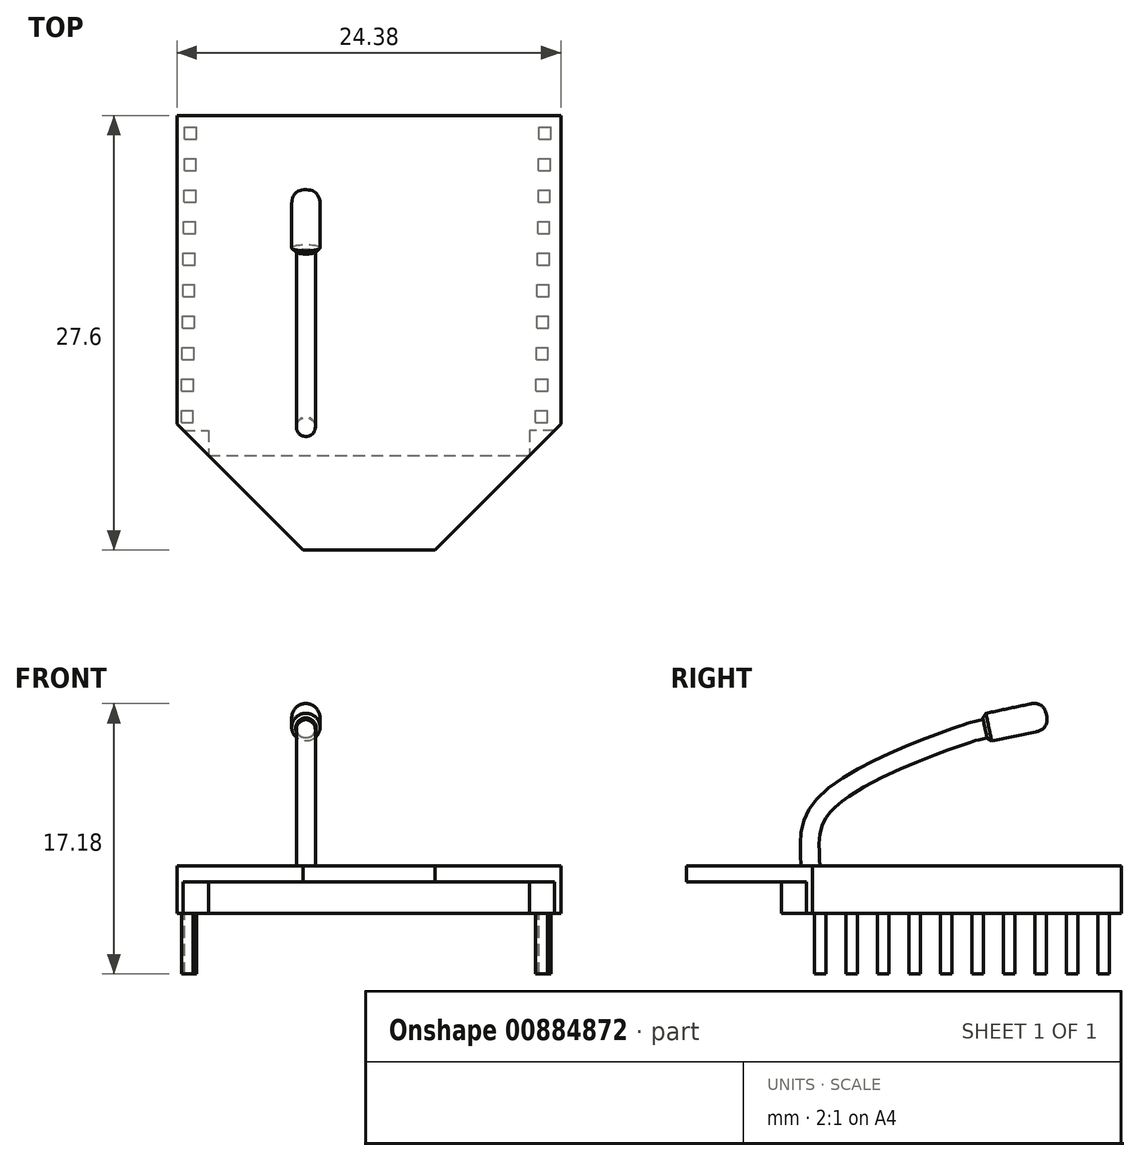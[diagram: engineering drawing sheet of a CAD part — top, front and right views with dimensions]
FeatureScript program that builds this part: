
annotation { "Feature Type Name" : "Feature", "Feature Type Description" : "" }
export const myFeature = defineFeature(function(context is Context, id is Id, definition is map)
    precondition{}
    {
        {
            var Q0;
            Q0=qCreatedBy(makeId("Top.planeOp"),FACE);
            var sketch = newSketch(context, id + "F0", { "sketchPlane" : qUnion([Q0])});
            skLineSegment(sketch, "E0.bottom", {"start": v(-12.19, 13.8) * mm, "end": v(12.2, 13.8) * mm});
            skLineSegment(sketch, "E0.top", {"start": v(-12.2, -13.8) * mm, "end": v(12.2, -13.8) * mm});
            skLineSegment(sketch, "E0.left", {"start": v(-12.19, 13.8) * mm, "end": v(-12.2, -13.8) * mm});
            skLineSegment(sketch, "E0.right", {"start": v(12.2, 13.8) * mm, "end": v(12.19, -13.8) * mm});
            skPoint(sketch, "E0.middle", {"position": v(0, 0) * mm});
            skSolve(sketch);
        }
        {
            var Q0;
            Q0=qSketchRegion(id+"F0",true);
            extrude(context, id + "F1", {"entities" : qUnion([Q0]), "oppositeDirection" : true, "depth" : 1 * mm, "offsetDistance" : 25 * mm});
        }
        {
            var Q0;
            Q0=makeQuery(id+"F1.opExtrude","CAP_FACE",FACE,{"disambiguationData":[OSD([sQuery(id+"F0.wireOp",EDGE,"E0.bottom"),sQuery(id+"F0.wireOp",EDGE,"E0.top"),sQuery(id+"F0.wireOp",EDGE,"E0.left"),sQuery(id+"F0.wireOp",EDGE,"E0.right")])],"isStart":false});
            var sketch = newSketch(context, id + "F2", { "sketchPlane" : qUnion([Q0])});
            skLineSegment(sketch, "E1.bottom", {"start": v(-12.19, -13.8) * mm, "end": v(-10.19, -13.8) * mm});
            skLineSegment(sketch, "E1.top", {"start": v(-12.2, 6.2) * mm, "end": v(-10.2, 6.2) * mm});
            skLineSegment(sketch, "E1.left", {"start": v(-12.19, -13.8) * mm, "end": v(-12.19, 6.2) * mm});
            skLineSegment(sketch, "E1.right", {"start": v(-10.19, -13.8) * mm, "end": v(-10.2, 6.2) * mm});
            skLineSegment(sketch, "E2.bottom", {"start": v(12.2, -13.8) * mm, "end": v(10.2, -13.8) * mm});
            skLineSegment(sketch, "E2.top", {"start": v(12.2, 6.2) * mm, "end": v(10.2, 6.2) * mm});
            skLineSegment(sketch, "E2.left", {"start": v(12.2, -13.8) * mm, "end": v(12.2, 6.2) * mm});
            skLineSegment(sketch, "E2.right", {"start": v(10.2, -13.8) * mm, "end": v(10.2, 6.2) * mm});
            skSolve(sketch);
        }
        {
            var Q0;
            Q0=makeQuery(id+"F2.imprint","IMPRINT",FACE,{"disambiguationData":[TD([[makeQuery(id+"F2.imprint","IMPRINT",EDGE,{"derivedFrom":sQuery(id+"F2.wireOp",EDGE,"E1.bottom")}),1.0]])]});
            var Q1;
            Q1=makeQuery(id+"F2.imprint","IMPRINT",FACE,{"disambiguationData":[TD([[makeQuery(id+"F2.imprint","IMPRINT",EDGE,{"derivedFrom":sQuery(id+"F2.wireOp",EDGE,"E2.bottom")}),1.0]])]});
            extrude(context, id + "F3", {"entities" : qUnion([Q0, Q1]), "operationType" : NewBodyOperationType.ADD, "depth" : 2 * mm, "offsetDistance" : 25 * mm});
        }
        {
            var Q0;
            Q0=makeQuery(id+"F3.opExtrude","CAP_FACE",FACE,{"disambiguationData":[OSD([sQuery(id+"F2.wireOp",EDGE,"E1.bottom"),sQuery(id+"F2.wireOp",EDGE,"E1.top"),sQuery(id+"F2.wireOp",EDGE,"E1.left"),sQuery(id+"F2.wireOp",EDGE,"E1.right")])],"isStart":false});
            var sketch = newSketch(context, id + "F4", { "sketchPlane" : qUnion([Q0])});
            skLineSegment(sketch, "E3.bottom", {"start": v(-11.69, -12.3) * mm, "end": v(-10.94, -12.3) * mm});
            skLineSegment(sketch, "E3.top", {"start": v(-11.69, -13.05) * mm, "end": v(-10.94, -13.05) * mm});
            skLineSegment(sketch, "E3.left", {"start": v(-11.69, -12.3) * mm, "end": v(-11.69, -13.05) * mm});
            skLineSegment(sketch, "E3.right", {"start": v(-10.94, -12.3) * mm, "end": v(-10.94, -13.05) * mm});
            skLineSegment(sketch, "E4.0.1.0", {"start": v(-11.71, -10.3) * mm, "end": v(-10.96, -10.3) * mm});
            skLineSegment(sketch, "E4.0.1.1", {"start": v(-10.96, -10.3) * mm, "end": v(-10.96, -11.06) * mm});
            skLineSegment(sketch, "E4.0.1.2", {"start": v(-11.71, -10.3) * mm, "end": v(-11.71, -11.06) * mm});
            skLineSegment(sketch, "E4.0.1.3", {"start": v(-11.71, -11.06) * mm, "end": v(-10.96, -11.06) * mm});
            skLineSegment(sketch, "E4.0.2.0", {"start": v(-11.74, -8.3) * mm, "end": v(-10.99, -8.3) * mm});
            skLineSegment(sketch, "E4.0.2.1", {"start": v(-10.99, -8.3) * mm, "end": v(-10.99, -9.06) * mm});
            skLineSegment(sketch, "E4.0.2.2", {"start": v(-11.74, -8.3) * mm, "end": v(-11.74, -9.06) * mm});
            skLineSegment(sketch, "E4.0.2.3", {"start": v(-11.74, -9.06) * mm, "end": v(-10.99, -9.06) * mm});
            skLineSegment(sketch, "E4.0.3.0", {"start": v(-11.76, -6.3) * mm, "end": v(-11.01, -6.3) * mm});
            skLineSegment(sketch, "E4.0.3.1", {"start": v(-11.01, -6.3) * mm, "end": v(-11.01, -7.06) * mm});
            skLineSegment(sketch, "E4.0.3.2", {"start": v(-11.76, -6.3) * mm, "end": v(-11.76, -7.06) * mm});
            skLineSegment(sketch, "E4.0.3.3", {"start": v(-11.76, -7.06) * mm, "end": v(-11.01, -7.06) * mm});
            skLineSegment(sketch, "E4.0.4.0", {"start": v(-11.79, -4.3) * mm, "end": v(-11.04, -4.3) * mm});
            skLineSegment(sketch, "E4.0.4.1", {"start": v(-11.04, -4.3) * mm, "end": v(-11.04, -5.06) * mm});
            skLineSegment(sketch, "E4.0.4.2", {"start": v(-11.79, -4.3) * mm, "end": v(-11.79, -5.06) * mm});
            skLineSegment(sketch, "E4.0.4.3", {"start": v(-11.79, -5.06) * mm, "end": v(-11.04, -5.06) * mm});
            skLineSegment(sketch, "E4.0.5.0", {"start": v(-11.81, -2.3) * mm, "end": v(-11.06, -2.3) * mm});
            skLineSegment(sketch, "E4.0.5.1", {"start": v(-11.06, -2.3) * mm, "end": v(-11.06, -3.06) * mm});
            skLineSegment(sketch, "E4.0.5.2", {"start": v(-11.81, -2.3) * mm, "end": v(-11.81, -3.06) * mm});
            skLineSegment(sketch, "E4.0.5.3", {"start": v(-11.81, -3.06) * mm, "end": v(-11.06, -3.06) * mm});
            skLineSegment(sketch, "E4.0.6.0", {"start": v(-11.83, -0.3) * mm, "end": v(-11.08, -0.3) * mm});
            skLineSegment(sketch, "E4.0.6.1", {"start": v(-11.08, -0.3) * mm, "end": v(-11.08, -1.06) * mm});
            skLineSegment(sketch, "E4.0.6.2", {"start": v(-11.83, -0.3) * mm, "end": v(-11.83, -1.06) * mm});
            skLineSegment(sketch, "E4.0.6.3", {"start": v(-11.83, -1.06) * mm, "end": v(-11.08, -1.06) * mm});
            skLineSegment(sketch, "E4.0.7.0", {"start": v(-11.86, 1.7) * mm, "end": v(-11.1, 1.7) * mm});
            skLineSegment(sketch, "E4.0.7.1", {"start": v(-11.1, 1.7) * mm, "end": v(-11.1, 0.94) * mm});
            skLineSegment(sketch, "E4.0.7.2", {"start": v(-11.86, 1.7) * mm, "end": v(-11.86, 0.94) * mm});
            skLineSegment(sketch, "E4.0.7.3", {"start": v(-11.86, 0.94) * mm, "end": v(-11.1, 0.94) * mm});
            skLineSegment(sketch, "E4.0.8.0", {"start": v(-11.88, 3.7) * mm, "end": v(-11.13, 3.7) * mm});
            skLineSegment(sketch, "E4.0.8.1", {"start": v(-11.13, 3.7) * mm, "end": v(-11.13, 2.94) * mm});
            skLineSegment(sketch, "E4.0.8.2", {"start": v(-11.88, 3.7) * mm, "end": v(-11.88, 2.94) * mm});
            skLineSegment(sketch, "E4.0.8.3", {"start": v(-11.88, 2.94) * mm, "end": v(-11.13, 2.94) * mm});
            skLineSegment(sketch, "E4.0.9.0", {"start": v(-11.9, 5.7) * mm, "end": v(-11.16, 5.7) * mm});
            skLineSegment(sketch, "E4.0.9.1", {"start": v(-11.16, 5.7) * mm, "end": v(-11.16, 4.94) * mm});
            skLineSegment(sketch, "E4.0.9.2", {"start": v(-11.9, 5.7) * mm, "end": v(-11.9, 4.94) * mm});
            skLineSegment(sketch, "E4.0.9.3", {"start": v(-11.9, 4.94) * mm, "end": v(-11.16, 4.94) * mm});
            skLineSegment(sketch, "E4.1.0.0", {"start": v(10.81, -12.3) * mm, "end": v(11.56, -12.3) * mm});
            skLineSegment(sketch, "E4.1.0.1", {"start": v(11.56, -12.3) * mm, "end": v(11.56, -13.05) * mm});
            skLineSegment(sketch, "E4.1.0.2", {"start": v(10.81, -12.3) * mm, "end": v(10.81, -13.05) * mm});
            skLineSegment(sketch, "E4.1.0.3", {"start": v(10.81, -13.05) * mm, "end": v(11.56, -13.05) * mm});
            skLineSegment(sketch, "E4.1.1.0", {"start": v(10.79, -10.3) * mm, "end": v(11.54, -10.3) * mm});
            skLineSegment(sketch, "E4.1.1.1", {"start": v(11.54, -10.3) * mm, "end": v(11.54, -11.06) * mm});
            skLineSegment(sketch, "E4.1.1.2", {"start": v(10.79, -10.3) * mm, "end": v(10.79, -11.06) * mm});
            skLineSegment(sketch, "E4.1.1.3", {"start": v(10.79, -11.06) * mm, "end": v(11.54, -11.06) * mm});
            skLineSegment(sketch, "E4.1.2.0", {"start": v(10.76, -8.3) * mm, "end": v(11.51, -8.3) * mm});
            skLineSegment(sketch, "E4.1.2.1", {"start": v(11.51, -8.3) * mm, "end": v(11.51, -9.06) * mm});
            skLineSegment(sketch, "E4.1.2.2", {"start": v(10.76, -8.3) * mm, "end": v(10.76, -9.06) * mm});
            skLineSegment(sketch, "E4.1.2.3", {"start": v(10.76, -9.06) * mm, "end": v(11.51, -9.06) * mm});
            skLineSegment(sketch, "E4.1.3.0", {"start": v(10.74, -6.3) * mm, "end": v(11.49, -6.3) * mm});
            skLineSegment(sketch, "E4.1.3.1", {"start": v(11.49, -6.3) * mm, "end": v(11.49, -7.06) * mm});
            skLineSegment(sketch, "E4.1.3.2", {"start": v(10.74, -6.3) * mm, "end": v(10.74, -7.06) * mm});
            skLineSegment(sketch, "E4.1.3.3", {"start": v(10.74, -7.06) * mm, "end": v(11.49, -7.06) * mm});
            skLineSegment(sketch, "E4.1.4.0", {"start": v(10.71, -4.3) * mm, "end": v(11.46, -4.3) * mm});
            skLineSegment(sketch, "E4.1.4.1", {"start": v(11.46, -4.3) * mm, "end": v(11.46, -5.06) * mm});
            skLineSegment(sketch, "E4.1.4.2", {"start": v(10.71, -4.3) * mm, "end": v(10.71, -5.06) * mm});
            skLineSegment(sketch, "E4.1.4.3", {"start": v(10.71, -5.06) * mm, "end": v(11.46, -5.06) * mm});
            skLineSegment(sketch, "E4.1.5.0", {"start": v(10.69, -2.3) * mm, "end": v(11.44, -2.3) * mm});
            skLineSegment(sketch, "E4.1.5.1", {"start": v(11.44, -2.3) * mm, "end": v(11.44, -3.06) * mm});
            skLineSegment(sketch, "E4.1.5.2", {"start": v(10.69, -2.3) * mm, "end": v(10.69, -3.06) * mm});
            skLineSegment(sketch, "E4.1.5.3", {"start": v(10.69, -3.06) * mm, "end": v(11.44, -3.06) * mm});
            skLineSegment(sketch, "E4.1.6.0", {"start": v(10.67, -0.3) * mm, "end": v(11.42, -0.3) * mm});
            skLineSegment(sketch, "E4.1.6.1", {"start": v(11.42, -0.3) * mm, "end": v(11.42, -1.06) * mm});
            skLineSegment(sketch, "E4.1.6.2", {"start": v(10.67, -0.3) * mm, "end": v(10.67, -1.06) * mm});
            skLineSegment(sketch, "E4.1.6.3", {"start": v(10.67, -1.06) * mm, "end": v(11.42, -1.06) * mm});
            skLineSegment(sketch, "E4.1.7.0", {"start": v(10.64, 1.7) * mm, "end": v(11.4, 1.7) * mm});
            skLineSegment(sketch, "E4.1.7.1", {"start": v(11.4, 1.7) * mm, "end": v(11.4, 0.94) * mm});
            skLineSegment(sketch, "E4.1.7.2", {"start": v(10.64, 1.7) * mm, "end": v(10.64, 0.94) * mm});
            skLineSegment(sketch, "E4.1.7.3", {"start": v(10.64, 0.94) * mm, "end": v(11.4, 0.94) * mm});
            skLineSegment(sketch, "E4.1.8.0", {"start": v(10.62, 3.7) * mm, "end": v(11.37, 3.7) * mm});
            skLineSegment(sketch, "E4.1.8.1", {"start": v(11.37, 3.7) * mm, "end": v(11.37, 2.94) * mm});
            skLineSegment(sketch, "E4.1.8.2", {"start": v(10.62, 3.7) * mm, "end": v(10.62, 2.94) * mm});
            skLineSegment(sketch, "E4.1.8.3", {"start": v(10.62, 2.94) * mm, "end": v(11.37, 2.94) * mm});
            skLineSegment(sketch, "E4.1.9.0", {"start": v(10.6, 5.7) * mm, "end": v(11.34, 5.7) * mm});
            skLineSegment(sketch, "E4.1.9.1", {"start": v(11.34, 5.7) * mm, "end": v(11.34, 4.94) * mm});
            skLineSegment(sketch, "E4.1.9.2", {"start": v(10.6, 5.7) * mm, "end": v(10.6, 4.94) * mm});
            skLineSegment(sketch, "E4.1.9.3", {"start": v(10.6, 4.94) * mm, "end": v(11.34, 4.94) * mm});
            skLineSegment(sketch, "E4.direction1", {"start": v(-11.69, -13.05) * mm, "end": v(10.81, -13.05) * mm, "construction": true});
            skLineSegment(sketch, "E4.direction2", {"start": v(-11.69, -13.05) * mm, "end": v(-11.71, -11.06) * mm, "construction": true});
            skSolve(sketch);
        }
        {
            var Q0;
            Q0=makeQuery(id+"F4.imprint","IMPRINT",FACE,{"disambiguationData":[TD([[makeQuery(id+"F4.imprint","IMPRINT",EDGE,{"derivedFrom":sQuery(id+"F4.wireOp",EDGE,"E3.bottom")}),-1.0]])]});
            var Q1;
            Q1=makeQuery(id+"F4.imprint","IMPRINT",FACE,{"disambiguationData":[TD([[makeQuery(id+"F4.imprint","IMPRINT",EDGE,{"derivedFrom":sQuery(id+"F4.wireOp",EDGE,"E4.0.1.0")}),-1.0]])]});
            var Q2;
            Q2=makeQuery(id+"F4.imprint","IMPRINT",FACE,{"disambiguationData":[TD([[makeQuery(id+"F4.imprint","IMPRINT",EDGE,{"derivedFrom":sQuery(id+"F4.wireOp",EDGE,"E4.0.2.0")}),-1.0]])]});
            var Q3;
            Q3=makeQuery(id+"F4.imprint","IMPRINT",FACE,{"disambiguationData":[TD([[makeQuery(id+"F4.imprint","IMPRINT",EDGE,{"derivedFrom":sQuery(id+"F4.wireOp",EDGE,"E4.0.3.0")}),-1.0]])]});
            var Q4;
            Q4=makeQuery(id+"F4.imprint","IMPRINT",FACE,{"disambiguationData":[TD([[makeQuery(id+"F4.imprint","IMPRINT",EDGE,{"derivedFrom":sQuery(id+"F4.wireOp",EDGE,"E4.0.4.0")}),-1.0]])]});
            var Q5;
            Q5=makeQuery(id+"F4.imprint","IMPRINT",FACE,{"disambiguationData":[TD([[makeQuery(id+"F4.imprint","IMPRINT",EDGE,{"derivedFrom":sQuery(id+"F4.wireOp",EDGE,"E4.0.5.0")}),-1.0]])]});
            var Q6;
            Q6=makeQuery(id+"F4.imprint","IMPRINT",FACE,{"disambiguationData":[TD([[makeQuery(id+"F4.imprint","IMPRINT",EDGE,{"derivedFrom":sQuery(id+"F4.wireOp",EDGE,"E4.0.6.0")}),-1.0]])]});
            var Q7;
            Q7=makeQuery(id+"F4.imprint","IMPRINT",FACE,{"disambiguationData":[TD([[makeQuery(id+"F4.imprint","IMPRINT",EDGE,{"derivedFrom":sQuery(id+"F4.wireOp",EDGE,"E4.0.7.0")}),-1.0]])]});
            var Q8;
            Q8=makeQuery(id+"F4.imprint","IMPRINT",FACE,{"disambiguationData":[TD([[makeQuery(id+"F4.imprint","IMPRINT",EDGE,{"derivedFrom":sQuery(id+"F4.wireOp",EDGE,"E4.0.8.0")}),-1.0]])]});
            var Q9;
            Q9=makeQuery(id+"F4.imprint","IMPRINT",FACE,{"disambiguationData":[TD([[makeQuery(id+"F4.imprint","IMPRINT",EDGE,{"derivedFrom":sQuery(id+"F4.wireOp",EDGE,"E4.0.9.0")}),-1.0]])]});
            var Q10;
            Q10=makeQuery(id+"F4.imprint","IMPRINT",FACE,{"disambiguationData":[TD([[makeQuery(id+"F4.imprint","IMPRINT",EDGE,{"derivedFrom":sQuery(id+"F4.wireOp",EDGE,"E4.1.9.0")}),-1.0]])]});
            var Q11;
            Q11=makeQuery(id+"F4.imprint","IMPRINT",FACE,{"disambiguationData":[TD([[makeQuery(id+"F4.imprint","IMPRINT",EDGE,{"derivedFrom":sQuery(id+"F4.wireOp",EDGE,"E4.1.8.0")}),-1.0]])]});
            var Q12;
            Q12=makeQuery(id+"F4.imprint","IMPRINT",FACE,{"disambiguationData":[TD([[makeQuery(id+"F4.imprint","IMPRINT",EDGE,{"derivedFrom":sQuery(id+"F4.wireOp",EDGE,"E4.1.7.0")}),-1.0]])]});
            var Q13;
            Q13=makeQuery(id+"F4.imprint","IMPRINT",FACE,{"disambiguationData":[TD([[makeQuery(id+"F4.imprint","IMPRINT",EDGE,{"derivedFrom":sQuery(id+"F4.wireOp",EDGE,"E4.1.6.0")}),-1.0]])]});
            var Q14;
            Q14=makeQuery(id+"F4.imprint","IMPRINT",FACE,{"disambiguationData":[TD([[makeQuery(id+"F4.imprint","IMPRINT",EDGE,{"derivedFrom":sQuery(id+"F4.wireOp",EDGE,"E4.1.5.0")}),-1.0]])]});
            var Q15;
            Q15=makeQuery(id+"F4.imprint","IMPRINT",FACE,{"disambiguationData":[TD([[makeQuery(id+"F4.imprint","IMPRINT",EDGE,{"derivedFrom":sQuery(id+"F4.wireOp",EDGE,"E4.1.4.0")}),-1.0]])]});
            var Q16;
            Q16=makeQuery(id+"F4.imprint","IMPRINT",FACE,{"disambiguationData":[TD([[makeQuery(id+"F4.imprint","IMPRINT",EDGE,{"derivedFrom":sQuery(id+"F4.wireOp",EDGE,"E4.1.3.0")}),-1.0]])]});
            var Q17;
            Q17=makeQuery(id+"F4.imprint","IMPRINT",FACE,{"disambiguationData":[TD([[makeQuery(id+"F4.imprint","IMPRINT",EDGE,{"derivedFrom":sQuery(id+"F4.wireOp",EDGE,"E4.1.2.0")}),-1.0]])]});
            var Q18;
            Q18=makeQuery(id+"F4.imprint","IMPRINT",FACE,{"disambiguationData":[TD([[makeQuery(id+"F4.imprint","IMPRINT",EDGE,{"derivedFrom":sQuery(id+"F4.wireOp",EDGE,"E4.1.1.0")}),-1.0]])]});
            var Q19;
            Q19=makeQuery(id+"F4.imprint","IMPRINT",FACE,{"disambiguationData":[TD([[makeQuery(id+"F4.imprint","IMPRINT",EDGE,{"derivedFrom":sQuery(id+"F4.wireOp",EDGE,"E4.1.0.0")}),-1.0]])]});
            extrude(context, id + "F5", {"entities" : qUnion([Q0, Q1, Q2, Q3, Q4, Q5, Q6, Q7, Q8, Q9, Q10, Q11, Q12, Q13, Q14, Q15, Q16, Q17, Q18, Q19]), "operationType" : NewBodyOperationType.ADD, "depth" : (6.86 - (1 + 2)) * mm, "offsetDistance" : 25 * mm});
        }
        {
            var Q0;
            Q0=makeQuery(id+"F1.opExtrude","SWEPT_EDGE",EDGE,{"disambiguationData":[OSD([sQuery(id+"F0.wireOp",EDGE,"E0.top"),sQuery(id+"F0.wireOp",EDGE,"E0.right")])]});
            var Q1;
            Q1=makeQuery(id+"F1.opExtrude","SWEPT_EDGE",EDGE,{"disambiguationData":[OSD([sQuery(id+"F0.wireOp",EDGE,"E0.top"),sQuery(id+"F0.wireOp",EDGE,"E0.left")])]});
            chamfer(context, id + "F6", {"entities" : qUnion([Q0, Q1]), "width" : 8 * mm, "tangentPropagation" : true});
        }
        {
            var Q0;
            Q0=makeQuery(id+"F1.opExtrude","CAP_FACE",FACE,{"disambiguationData":[OSD([sQuery(id+"F0.wireOp",EDGE,"E0.bottom"),sQuery(id+"F0.wireOp",EDGE,"E0.top"),sQuery(id+"F0.wireOp",EDGE,"E0.left"),sQuery(id+"F0.wireOp",EDGE,"E0.right")])],"isStart":false});
            var sketch = newSketch(context, id + "F7", { "sketchPlane" : qUnion([Q0])});
            skLineSegment(sketch, "E5.bottom", {"start": v(-10.19, -13.8) * mm, "end": v(10.2, -13.8) * mm});
            skLineSegment(sketch, "E5.top", {"start": v(-10.19, 7.8) * mm, "end": v(10.2, 7.8) * mm});
            skLineSegment(sketch, "E5.left", {"start": v(-10.2, -13.8) * mm, "end": v(-10.2, 7.8) * mm});
            skLineSegment(sketch, "E5.right", {"start": v(10.2, -13.8) * mm, "end": v(10.2, 7.8) * mm});
            skSolve(sketch);
        }
        {
            var Q0;
            {var subQ2=sQuery(id+"F7.wireOp",EDGE,"E5.top");Q0=makeQuery(id+"F7.imprint","IMPRINT",FACE,{"disambiguationData":[TD([[makeQuery(id+"F7.imprint","IMPRINT",EDGE,{"derivedFrom":subQ2}),-1.0]])]});}
            extrude(context, id + "F8", {"entities" : qUnion([Q0]), "operationType" : NewBodyOperationType.ADD, "depth" : 2 * mm, "offsetDistance" : 25 * mm});
        }
        {
            var Q0;
            Q0=qCreatedBy(makeId("Right.planeOp"),FACE);
            cPlane(context, id + "F9", {"entities" : qUnion([Q0]), "cplaneType" : CPlaneType.OFFSET, "offset" : 4 * mm, "oppositeDirection" : true, "width" : 150 * mm, "height" : 150 * mm});
        }
        {
            var Q0;
            Q0=qCreatedBy(id+"F9.planeOp",FACE);
            var sketch = newSketch(context, id + "F10", { "sketchPlane" : qUnion([Q0])});
            skFitSpline(sketch, "E6", {"points": [v(-5.95, 0) * mm, v(-4.96, 4) * mm, v(3.85, 8.37) * mm, v(9.06, 9.6) * mm], "startDerivative": vector(-0.35, 15.25) * mm, "endDerivative": vector(50.53, 11.9) * mm});
            skSolve(sketch);
        }
        {
            var Q0;
            Q0=makeQuery(id+"F1.opExtrude","CAP_FACE",FACE,{"disambiguationData":[OSD([sQuery(id+"F0.wireOp",EDGE,"E0.bottom"),sQuery(id+"F0.wireOp",EDGE,"E0.top"),sQuery(id+"F0.wireOp",EDGE,"E0.left"),sQuery(id+"F0.wireOp",EDGE,"E0.right")])],"isStart":true});
            var sketch = newSketch(context, id + "F11", { "sketchPlane" : qUnion([Q0])});
            skCircle(sketch, "E7", {"center": v(-4, -5.95) * mm, "radius": 0.6 * mm});
            skSolve(sketch);
        }
        {
            var Q0;
            Q0=makeQuery(id+"F11.imprint","IMPRINT",FACE,{"disambiguationData":[TD([[makeQuery(id+"F11.imprint","IMPRINT",EDGE,{"derivedFrom":sQuery(id+"F11.wireOp",EDGE,"E7")}),1.0]])]});
            var Q1;
            Q1=sQuery(id+"F10.wireOp",EDGE,"E6");
            sweep(context, id + "F12", {"operationType" : NewBodyOperationType.ADD, "profiles" : qUnion([Q0]), "path" : qUnion([Q1])});
        }
        {
            var Q0;
            Q0=makeQuery(id+"F12.opSweep","CAP_FACE",FACE,{"disambiguationData":[OSD([sQuery(id+"F10.wireOp",VERTEX,"E6.end"),sQuery(id+"F11.wireOp",EDGE,"E7")])],"isStart":false});
            var sketch = newSketch(context, id + "F13", { "sketchPlane" : qUnion([Q0])});
            skCircle(sketch, "E8", {"center": v(4, 7.51) * mm, "radius": 0.9 * mm});
            skSolve(sketch);
        }
        {
            var Q0;
            Q0=makeQuery(id+"F13.imprint","IMPRINT",FACE,{"disambiguationData":[TD([[makeQuery(id+"F13.imprint","IMPRINT",EDGE,{"derivedFrom":sQuery(id+"F13.wireOp",EDGE,"E8")}),1.0]])]});
            var Q1;
            Q1=makeQuery(id+"F13.imprint","IMPRINT",FACE,{"disambiguationData":[TD([[makeQuery(id+"F13.imprint","IMPRINT",EDGE,{"derivedFrom":makeQuery(id+"F12.opSweep","CAP_EDGE",EDGE,{"disambiguationData":[OSD([sQuery(id+"F10.wireOp",VERTEX,"E6.end"),sQuery(id+"F11.wireOp",EDGE,"E7")])],"isStart":false})}),1.0]])]});
            extrude(context, id + "F14", {"entities" : qUnion([Q0, Q1]), "operationType" : NewBodyOperationType.ADD, "oppositeDirection" : true, "depth" : 4 * mm, "offsetDistance" : 25 * mm});
        }
        {
            var Q0;
            Q0=makeQuery(id+"F14.opExtrude","CAP_EDGE",EDGE,{"disambiguationData":[OSD([sQuery(id+"F13.wireOp",EDGE,"E8")])],"isStart":true});
            fillet(context, id + "F15", {"entities" : qUnion([Q0]), "radius" : 0.9 * mm, "rho" : 0.5, "crossSection" : FilletCrossSection.CONIC, "allowEdgeOverflow" : false});
        }
        {
            var Q0;
            Q0=makeQuery(id+"F14.opExtrude","CAP_EDGE",EDGE,{"disambiguationData":[OSD([sQuery(id+"F13.wireOp",EDGE,"E8")])],"isStart":false});
            chamfer(context, id + "F16", {"entities" : qUnion([Q0]), "width" : .25 * mm, "tangentPropagation" : true});
        }
    });
